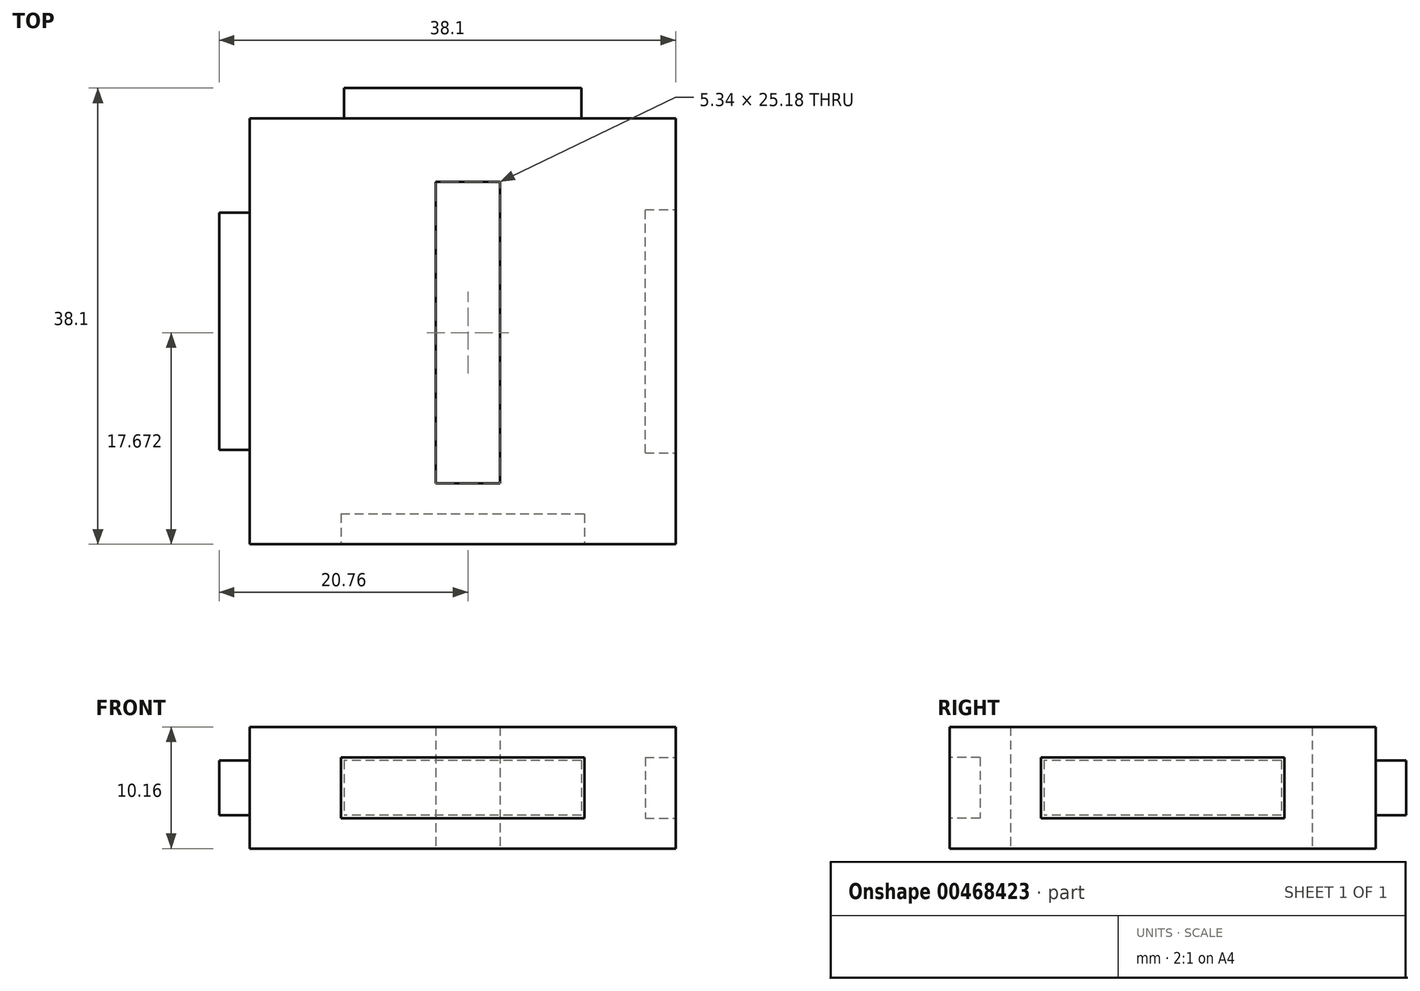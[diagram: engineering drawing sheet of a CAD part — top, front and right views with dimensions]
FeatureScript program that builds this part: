
annotation { "Feature Type Name" : "Feature", "Feature Type Description" : "" }
export const myFeature = defineFeature(function(context is Context, id is Id, definition is map)
    precondition{}
    {
        {
            var Q0;
            Q0=qCreatedBy(makeId("Top.planeOp"),FACE);
            var sketch = newSketch(context, id + "F0", { "sketchPlane" : qUnion([Q0])});
            skLineSegment(sketch, "E0.bottom", {"start": v(-17.78, 17.78) * mm, "end": v(17.78, 17.78) * mm});
            skLineSegment(sketch, "E0.top", {"start": v(-17.78, -17.78) * mm, "end": v(17.78, -17.78) * mm});
            skLineSegment(sketch, "E0.left", {"start": v(-17.78, 17.78) * mm, "end": v(-17.78, -17.78) * mm});
            skLineSegment(sketch, "E0.right", {"start": v(17.78, 17.78) * mm, "end": v(17.78, -17.78) * mm});
            skText(sketch, "E1", { "text": "I", "fontName": "OpenSans-Bold.ttf"});
            const initialGuessF0  = {"E1": [-0.0054, -0.0127, 1, 0, 0.0254]};
            skSetInitialGuess(sketch, initialGuessF0);
            skSolve(sketch);
        }
        {
            var Q0;
            Q0=qSketchRegion(id+"F0",true);
            extrude(context, id + "F1", {"entities" : qUnion([Q0]), "endBound" : BoundingType.SYMMETRIC, "depth" : 10.16 * mm});
        }
        {
            var Q0;
            Q0=makeQuery(id+"F1.opExtrude","SWEPT_FACE",FACE,{"disambiguationData":[OSD([sQuery(id+"F0.wireOp",EDGE,"E0.bottom")])]});
            var sketch = newSketch(context, id + "F2", { "sketchPlane" : qUnion([Q0])});
            skLineSegment(sketch, "E2.bottom", {"start": v(-9.9, 2.29) * mm, "end": v(9.9, 2.29) * mm});
            skLineSegment(sketch, "E2.top", {"start": v(-9.9, -2.29) * mm, "end": v(9.9, -2.29) * mm});
            skLineSegment(sketch, "E2.left", {"start": v(-9.9, 2.29) * mm, "end": v(-9.9, -2.29) * mm});
            skLineSegment(sketch, "E2.right", {"start": v(9.9, 2.29) * mm, "end": v(9.9, -2.29) * mm});
            skSolve(sketch);
        }
        {
            var Q0;
            Q0=qSketchRegion(id+"F2",true);
            extrude(context, id + "F3", {"entities" : qUnion([Q0]), "operationType" : NewBodyOperationType.ADD, "depth" : 2.54 * mm});
        }
        {
            var Q0;
            Q0=makeQuery(id+"F1.opExtrude","SWEPT_FACE",FACE,{"disambiguationData":[OSD([sQuery(id+"F0.wireOp",EDGE,"E0.left")])]});
            var sketch = newSketch(context, id + "F4", { "sketchPlane" : qUnion([Q0])});
            skLineSegment(sketch, "E3.bottom", {"start": v(-9.9, 2.29) * mm, "end": v(9.9, 2.29) * mm});
            skLineSegment(sketch, "E3.top", {"start": v(-9.9, -2.29) * mm, "end": v(9.9, -2.29) * mm});
            skLineSegment(sketch, "E3.left", {"start": v(-9.9, 2.29) * mm, "end": v(-9.9, -2.29) * mm});
            skLineSegment(sketch, "E3.right", {"start": v(9.9, 2.29) * mm, "end": v(9.9, -2.29) * mm});
            skSolve(sketch);
        }
        {
            var Q0;
            Q0=qSketchRegion(id+"F4",true);
            extrude(context, id + "F5", {"entities" : qUnion([Q0]), "operationType" : NewBodyOperationType.ADD, "depth" : 2.54 * mm});
        }
        {
            var Q0;
            Q0=makeQuery(id+"F1.opExtrude","SWEPT_FACE",FACE,{"disambiguationData":[OSD([sQuery(id+"F0.wireOp",EDGE,"E0.top")])]});
            var sketch = newSketch(context, id + "F6", { "sketchPlane" : qUnion([Q0])});
            skLineSegment(sketch, "E4.bottom", {"start": v(-10.16, 2.54) * mm, "end": v(10.16, 2.54) * mm});
            skLineSegment(sketch, "E4.top", {"start": v(-10.16, -2.54) * mm, "end": v(10.16, -2.54) * mm});
            skLineSegment(sketch, "E4.left", {"start": v(-10.16, 2.54) * mm, "end": v(-10.16, -2.54) * mm});
            skLineSegment(sketch, "E4.right", {"start": v(10.16, 2.54) * mm, "end": v(10.16, -2.54) * mm});
            skSolve(sketch);
        }
        {
            var Q0;
            Q0=qSketchRegion(id+"F6",true);
            extrude(context, id + "F7", {"entities" : qUnion([Q0]), "operationType" : NewBodyOperationType.REMOVE, "oppositeDirection" : true, "depth" : 2.54 * mm});
        }
        {
            var Q0;
            Q0=makeQuery(id+"F1.opExtrude","SWEPT_FACE",FACE,{"disambiguationData":[OSD([sQuery(id+"F0.wireOp",EDGE,"E0.right")])]});
            var sketch = newSketch(context, id + "F8", { "sketchPlane" : qUnion([Q0])});
            skLineSegment(sketch, "E5.bottom", {"start": v(-10.16, 2.54) * mm, "end": v(10.16, 2.54) * mm});
            skLineSegment(sketch, "E5.top", {"start": v(-10.16, -2.54) * mm, "end": v(10.16, -2.54) * mm});
            skLineSegment(sketch, "E5.left", {"start": v(-10.16, 2.54) * mm, "end": v(-10.16, -2.54) * mm});
            skLineSegment(sketch, "E5.right", {"start": v(10.16, 2.54) * mm, "end": v(10.16, -2.54) * mm});
            skSolve(sketch);
        }
        {
            var Q0;
            Q0=qSketchRegion(id+"F8",true);
            extrude(context, id + "F9", {"entities" : qUnion([Q0]), "operationType" : NewBodyOperationType.REMOVE, "oppositeDirection" : true, "depth" : 2.54 * mm});
        }
    });
